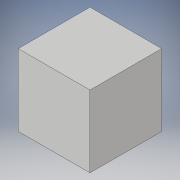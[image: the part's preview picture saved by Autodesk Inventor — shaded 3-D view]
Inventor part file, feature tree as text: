
AUTODESK INVENTOR PART (.ipt)
format: ipt  version: 2017 (Build 210142000, 142)  size: 82,944 bytes
history: native  units: in
note: dims shown in document units (in); Inventor stores cm internally (conversion verified against a paired STEP export)
features: extrude x1, sketch x1
ambient origin geometry x8: Origin, YZ Plane, XZ Plane, XY Plane, X Axis, Y Axis, Z Axis, Center Point
bodies: Solid1 (feature_tree)
feature tree (2):
  extrude  "Extrusion1"  Depth=6.0in
  sketch  "Sketch1"  dims[d0=6.0in d1=6.0in d2=6.0in d3=0.0in]
